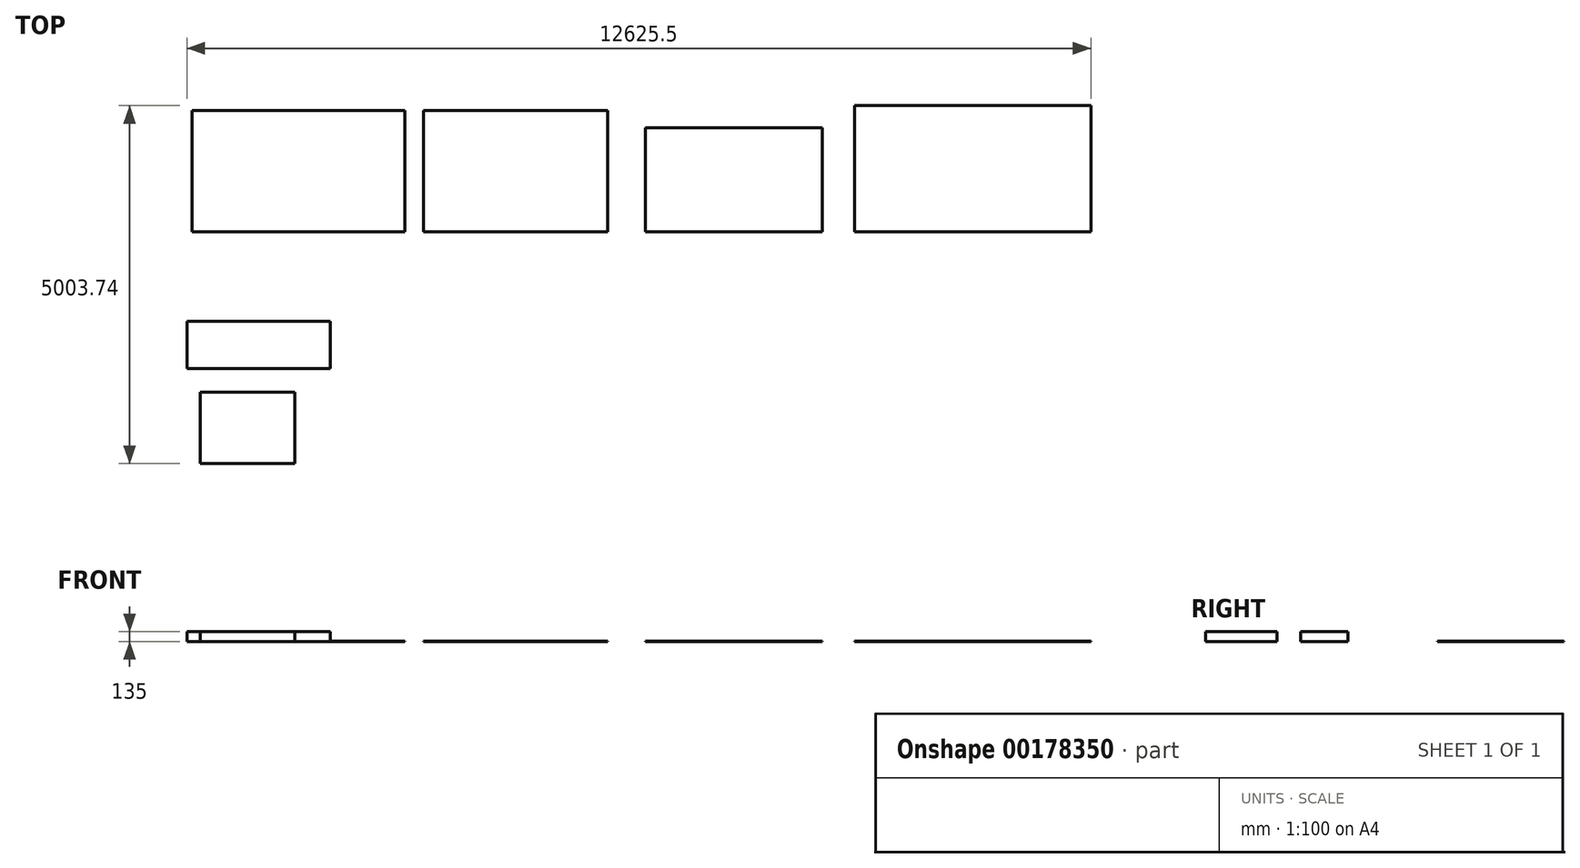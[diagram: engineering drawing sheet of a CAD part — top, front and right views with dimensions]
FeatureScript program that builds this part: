
annotation { "Feature Type Name" : "Feature", "Feature Type Description" : "" }
export const myFeature = defineFeature(function(context is Context, id is Id, definition is map)
    precondition{}
    {
        {
            var Q0;
            Q0=qCreatedBy(makeId("Top.planeOp"),FACE);
            var sketch = newSketch(context, id + "F0", { "sketchPlane" : qUnion([Q0])});
            skLineSegment(sketch, "E0.bottom", {"start": v(-68.47, 50.72) * mm, "end": v(2901.53, 50.72) * mm});
            skLineSegment(sketch, "E0.top", {"start": v(-68.47, 1742.72) * mm, "end": v(2901.53, 1742.72) * mm});
            skLineSegment(sketch, "E0.left", {"start": v(-68.47, 50.72) * mm, "end": v(-68.47, 1742.72) * mm});
            skLineSegment(sketch, "E0.right", {"start": v(2901.53, 50.72) * mm, "end": v(2901.53, 1742.72) * mm});
            skLineSegment(sketch, "E1.bottom", {"start": v(3164.04, 1742.72) * mm, "end": v(5734.04, 1742.72) * mm});
            skLineSegment(sketch, "E1.top", {"start": v(3164.04, 50.72) * mm, "end": v(5734.04, 50.72) * mm});
            skLineSegment(sketch, "E1.left", {"start": v(3164.04, 1742.72) * mm, "end": v(3164.04, 50.72) * mm});
            skLineSegment(sketch, "E1.right", {"start": v(5734.04, 1742.72) * mm, "end": v(5734.04, 50.72) * mm});
            skText(sketch, "E2", { "text": "T5 long", "fontName": "OpenSans-Regular.ttf"});
            skText(sketch, "E3", { "text": "T5 short", "fontName": "OpenSans-Regular.ttf"});
            skText(sketch, "E4", { "text": "Low roof = 1410\nHigh roof = 1626", "fontName": "OpenSans-Regular.ttf"});
            skLineSegment(sketch, "E5.bottom", {"start": v(6260.85, 50.72) * mm, "end": v(8730.85, 50.72) * mm});
            skLineSegment(sketch, "E5.top", {"start": v(6260.85, 1500.72) * mm, "end": v(8730.85, 1500.72) * mm});
            skLineSegment(sketch, "E5.left", {"start": v(6260.85, 50.72) * mm, "end": v(6260.85, 1500.72) * mm});
            skLineSegment(sketch, "E5.right", {"start": v(8730.85, 50.72) * mm, "end": v(8730.85, 1500.72) * mm});
            skText(sketch, "E6", { "text": "Astro height 1200", "fontName": "OpenSans-Regular.ttf"});
            skLineSegment(sketch, "E7.bottom", {"start": v(9185.63, 50.72) * mm, "end": v(12485.63, 50.72) * mm});
            skLineSegment(sketch, "E7.top", {"start": v(9185.63, 1812.72) * mm, "end": v(12485.63, 1812.72) * mm});
            skLineSegment(sketch, "E7.left", {"start": v(9185.63, 50.72) * mm, "end": v(9185.63, 1812.72) * mm});
            skLineSegment(sketch, "E7.right", {"start": v(12485.63, 50.72) * mm, "end": v(12485.63, 1812.72) * mm});
            skText(sketch, "E8", { "text": "Transit long", "fontName": "OpenSans-Regular.ttf"});
            skLineSegment(sketch, "E9.bottom", {"start": v(-139.82, -1203.12) * mm, "end": v(1860.18, -1203.12) * mm});
            skLineSegment(sketch, "E9.top", {"start": v(-139.82, -1863.12) * mm, "end": v(1860.18, -1863.12) * mm});
            skLineSegment(sketch, "E9.left", {"start": v(-139.82, -1203.12) * mm, "end": v(-139.82, -1863.12) * mm});
            skLineSegment(sketch, "E9.right", {"start": v(1860.18, -1203.12) * mm, "end": v(1860.18, -1863.12) * mm});
            skLineSegment(sketch, "E10.bottom", {"start": v(45.02, -2191.02) * mm, "end": v(1365.02, -2191.02) * mm});
            skLineSegment(sketch, "E10.top", {"start": v(45.02, -3191.02) * mm, "end": v(1365.02, -3191.02) * mm});
            skLineSegment(sketch, "E10.left", {"start": v(45.02, -2191.02) * mm, "end": v(45.02, -3191.02) * mm});
            skLineSegment(sketch, "E10.right", {"start": v(1365.02, -2191.02) * mm, "end": v(1365.02, -3191.02) * mm});
            const initialGuessF0  = {"E2": [0.92132, 2.08762, 1, 0, 0.19623], "E3": [3.9319, 2.03598, 1, 0, 0.19107], "E4": [2.12463, 2.59885, 1, 0, 0.1291], "E6": [6.5891, 1.64353, 1, 0, 0.1724], "E8": [9.83535, 1.95476, 1, 0, 0.26814]};
            skSetInitialGuess(sketch, initialGuessF0);
            skSolve(sketch);
        }
        {
            var Q0;
            Q0=makeQuery(id+"F0.imprint","IMPRINT",FACE,{"disambiguationData":[TD([[makeQuery(id+"F0.imprint","IMPRINT",EDGE,{"derivedFrom":sQuery(id+"F0.wireOp",EDGE,"E0.bottom")}),1.0]])]});
            var Q1;
            Q1=makeQuery(id+"F0.imprint","IMPRINT",FACE,{"disambiguationData":[TD([[makeQuery(id+"F0.imprint","IMPRINT",EDGE,{"derivedFrom":sQuery(id+"F0.wireOp",EDGE,"E1.bottom")}),-1.0]])]});
            var Q2;
            Q2=makeQuery(id+"F0.imprint","IMPRINT",FACE,{"disambiguationData":[TD([[makeQuery(id+"F0.imprint","IMPRINT",EDGE,{"derivedFrom":sQuery(id+"F0.wireOp",EDGE,"E5.bottom")}),1.0]])]});
            var Q3;
            Q3=makeQuery(id+"F0.imprint","IMPRINT",FACE,{"disambiguationData":[TD([[makeQuery(id+"F0.imprint","IMPRINT",EDGE,{"derivedFrom":sQuery(id+"F0.wireOp",EDGE,"E7.bottom")}),1.0]])]});
            extrude(context, id + "F1", {"entities" : qUnion([Q0, Q1, Q2, Q3]), "depth" : 5 * mm});
        }
        {
            var Q0;
            Q0=makeQuery(id+"F0.imprint","IMPRINT",FACE,{"disambiguationData":[TD([[makeQuery(id+"F0.imprint","IMPRINT",EDGE,{"derivedFrom":sQuery(id+"F0.wireOp",EDGE,"E9.bottom")}),-1.0]])]});
            var Q1;
            Q1=makeQuery(id+"F0.imprint","IMPRINT",FACE,{"disambiguationData":[TD([[makeQuery(id+"F0.imprint","IMPRINT",EDGE,{"derivedFrom":sQuery(id+"F0.wireOp",EDGE,"E10.bottom")}),-1.0]])]});
            extrude(context, id + "F2", {"entities" : qUnion([Q0, Q1]), "depth" : 135 * mm});
        }
    });
